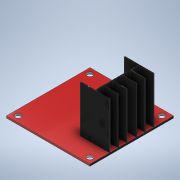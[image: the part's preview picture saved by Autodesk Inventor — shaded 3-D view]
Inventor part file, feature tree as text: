
AUTODESK INVENTOR PART (.ipt)
format: ipt  version: 2022 (Build 260153000, 153)  size: 182,272 bytes
history: native  units: in
note: dims shown in document units (in); Inventor stores cm internally (conversion verified against a paired STEP export)
features: extrude x3, sketch x3
ambient origin geometry x8: Origin, YZ Plane, XZ Plane, XY Plane, X Axis, Y Axis, Z Axis, Center Point
bodies: Solid1 (feature_tree)
feature tree (6):
  extrude  "Extrusion1"  Depth=1.6929in
  extrude  "Extrusion2"  Depth=0.0394in
  extrude  "Extrusion3"  Depth=0.9449in
  sketch  "Sketch1"  dims[d0=1.6929in d1=1.6929in]
  sketch  "Sketch2"  dims[d2=0.0394in d3=0.0in d4=0.1181in]
  sketch  "Sketch3"  dims[d5=0.1181in d6=0.1181in d7=1.5748in d9=360.0deg d11=0.0in d12=0.0in d13=0.3937in d14=0.3937in d15=0.9055in d16=0.5906in d17=0.1732in d18=0.1732in d19=0.1732in d20=0.1732in d22=0.0157in d23=0.0157in d24=0.0157in d25=0.0157in d26=0.0157in d27=0.0157in d28=0.0079in d29=0.0157in d30=0.9449in d31=0.0in]
